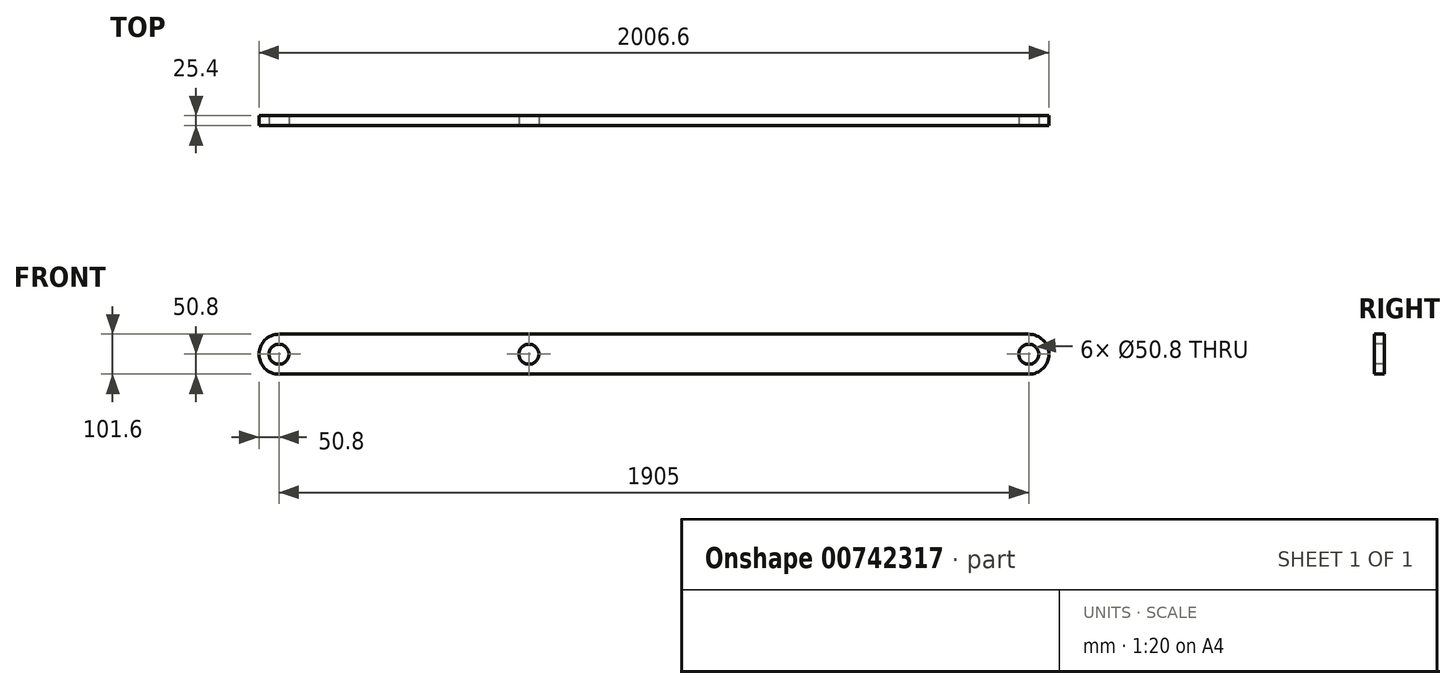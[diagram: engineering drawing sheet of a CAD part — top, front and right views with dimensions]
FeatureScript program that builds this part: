
annotation { "Feature Type Name" : "Feature", "Feature Type Description" : "" }
export const myFeature = defineFeature(function(context is Context, id is Id, definition is map)
    precondition{}
    {
        {
            var Q0;
            Q0=qCreatedBy(makeId("Front.planeOp"),FACE);
            var sketch = newSketch(context, id + "F0", { "sketchPlane" : qUnion([Q0])});
            skLineSegment(sketch, "E0.bottom", {"start": v(-952.5, 50.8) * mm, "end": v(952.5, 50.8) * mm});
            skLineSegment(sketch, "E0.top", {"start": v(-952.5, -50.8) * mm, "end": v(952.5, -50.8) * mm});
            skArc(sketch, "E1", {"start": v(-952.5, 50.8) * mm, "mid": v(-1003.3, 0) * mm, "end": v(-952.5, -50.8) * mm});
            skArc(sketch, "E2", {"start": v(952.5, -50.8) * mm, "mid": v(1003.3, 0) * mm, "end": v(952.5, 50.8) * mm});
            skSolve(sketch);
        }
        {
            var Q0;
            Q0=qSketchRegion(id+"F0",true);
            extrude(context, id + "F1", {"entities" : qUnion([Q0]), "endBound" : BoundingType.SYMMETRIC, "depth" : 25.4 * mm, "offsetDistance" : 25.4 * mm});
        }
        {
            var Q0;
            Q0=makeQuery(id+"F1.opExtrude","CAP_FACE",FACE,{"disambiguationData":[OSD([sQuery(id+"F0.wireOp",EDGE,"E0.bottom"),sQuery(id+"F0.wireOp",EDGE,"E0.top"),sQuery(id+"F0.wireOp",EDGE,"E1"),sQuery(id+"F0.wireOp",EDGE,"E2")])],"isStart":false});
            var sketch = newSketch(context, id + "F2", { "sketchPlane" : qUnion([Q0])});
            skCircle(sketch, "E3", {"center": v(-952.5, 0) * mm, "radius": 25.4 * mm});
            skCircle(sketch, "E4", {"center": v(952.5, 0) * mm, "radius": 25.4 * mm});
            skCircle(sketch, "E5", {"center": v(-317.5, 0) * mm, "radius": 25.4 * mm});
            skSolve(sketch);
        }
        {
            var Q0;
            Q0=qSketchRegion(id+"F2",true);
            extrude(context, id + "F3", {"entities" : qUnion([Q0]), "operationType" : NewBodyOperationType.REMOVE, "endBound" : BoundingType.THROUGH_ALL, "oppositeDirection" : true, "depth" : 25.4 * mm, "offsetDistance" : 25.4 * mm});
        }
    });
